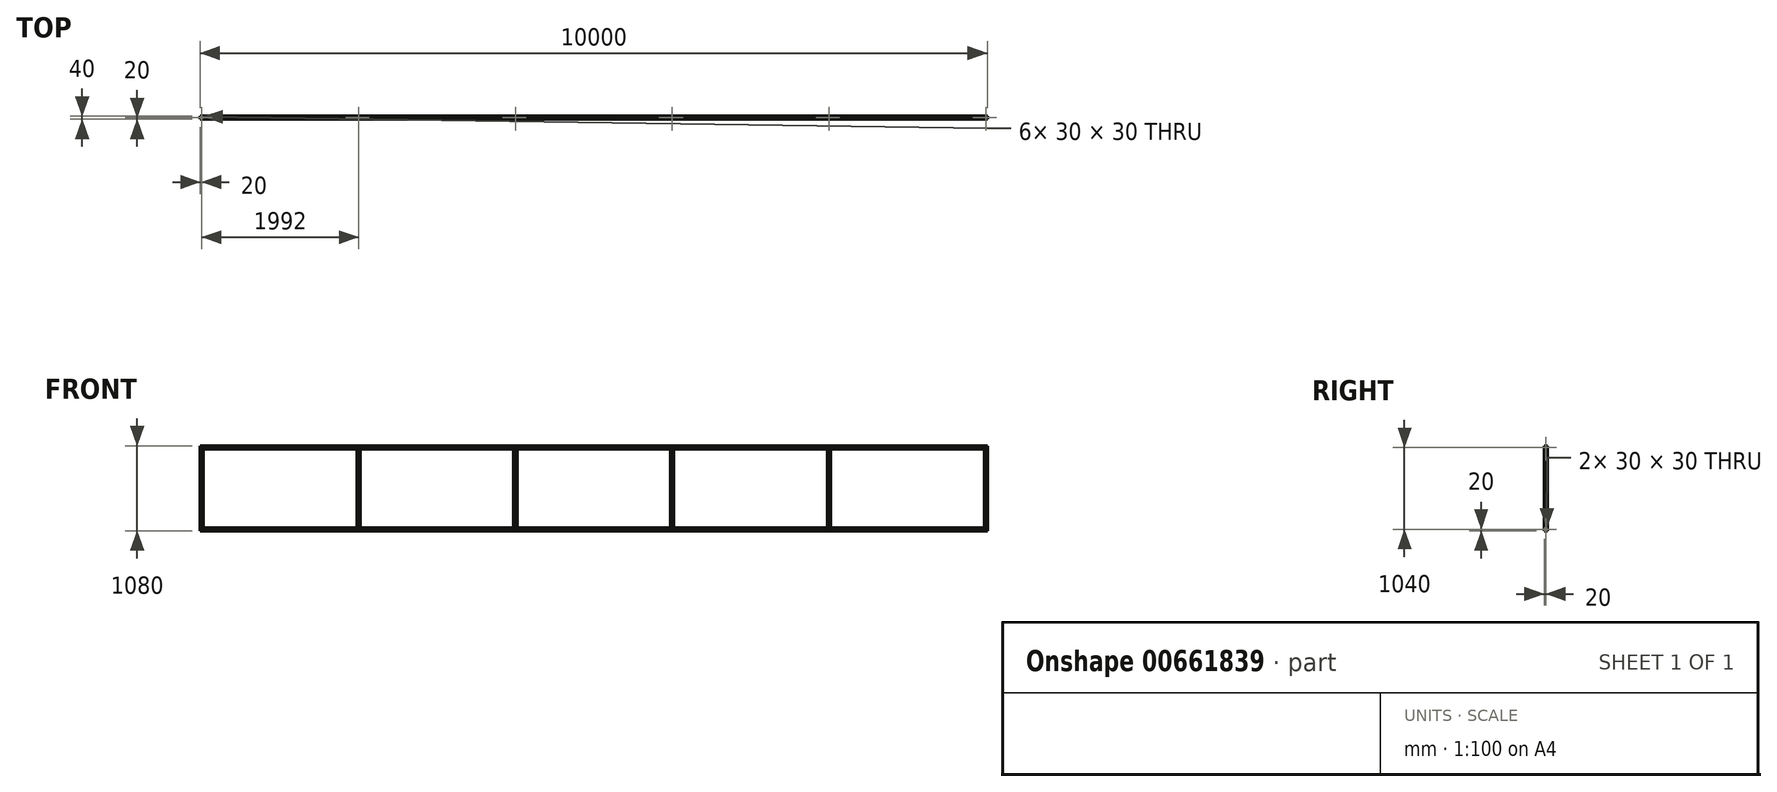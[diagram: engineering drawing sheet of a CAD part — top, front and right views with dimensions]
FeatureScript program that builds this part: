
annotation { "Feature Type Name" : "Feature", "Feature Type Description" : "" }
export const myFeature = defineFeature(function(context is Context, id is Id, definition is map)
    precondition{}
    {
        {
            var Q0;
            Q0=qCreatedBy(makeId("Top.planeOp"),FACE);
            var sketch = newSketch(context, id + "F0", { "sketchPlane" : qUnion([Q0])});
            skLineSegment(sketch, "E0", {"start": v(0, 0) * mm, "end": v(-5000, 0) * mm, "construction": true});
            skLineSegment(sketch, "E1", {"start": v(0, 0) * mm, "end": v(5000, 0) * mm, "construction": true});
            skLineSegment(sketch, "E2", {"start": v(-5000, 0) * mm, "end": v(-5000, 482.39) * mm, "construction": true});
            skLineSegment(sketch, "E3", {"start": v(5000, 0) * mm, "end": v(5000, 482.39) * mm, "construction": true});
            skLineSegment(sketch, "E4.bottom", {"start": v(-5000, 0) * mm, "end": v(-4960, 0) * mm});
            skLineSegment(sketch, "E4.top", {"start": v(-5000, -40) * mm, "end": v(-4960, -40) * mm});
            skLineSegment(sketch, "E4.left", {"start": v(-5000, 0) * mm, "end": v(-5000, -40) * mm});
            skLineSegment(sketch, "E4.right", {"start": v(-4960, 0) * mm, "end": v(-4960, -40) * mm});
            skLineSegment(sketch, "E5.0", {"start": v(-4995, -5) * mm, "end": v(-4965, -5) * mm});
            skLineSegment(sketch, "E5.1", {"start": v(-4995, -5) * mm, "end": v(-4995, -35) * mm});
            skLineSegment(sketch, "E5.2", {"start": v(-4995, -35) * mm, "end": v(-4965, -35) * mm});
            skLineSegment(sketch, "E5.3", {"start": v(-4965, -5) * mm, "end": v(-4965, -35) * mm});
            skLineSegment(sketch, "E6.1.0.0", {"start": v(-3008, -40) * mm, "end": v(-2968, -40) * mm});
            skLineSegment(sketch, "E6.1.0.1", {"start": v(-3008, 0) * mm, "end": v(-3008, -40) * mm});
            skLineSegment(sketch, "E6.1.0.2", {"start": v(-2968, 0) * mm, "end": v(-2968, -40) * mm});
            skLineSegment(sketch, "E6.1.0.3", {"start": v(-3008, 0) * mm, "end": v(-2968, 0) * mm});
            skLineSegment(sketch, "E6.1.0.4", {"start": v(-3003, -5) * mm, "end": v(-2973, -5) * mm});
            skLineSegment(sketch, "E6.1.0.5", {"start": v(-3003, -5) * mm, "end": v(-3003, -35) * mm});
            skLineSegment(sketch, "E6.1.0.6", {"start": v(-3003, -35) * mm, "end": v(-2973, -35) * mm});
            skLineSegment(sketch, "E6.1.0.7", {"start": v(-2973, -5) * mm, "end": v(-2973, -35) * mm});
            skLineSegment(sketch, "E6.2.0.0", {"start": v(-1016, -40) * mm, "end": v(-976, -40) * mm});
            skLineSegment(sketch, "E6.2.0.1", {"start": v(-1016, 0) * mm, "end": v(-1016, -40) * mm});
            skLineSegment(sketch, "E6.2.0.2", {"start": v(-976, 0) * mm, "end": v(-976, -40) * mm});
            skLineSegment(sketch, "E6.2.0.3", {"start": v(-1016, 0) * mm, "end": v(-976, 0) * mm});
            skLineSegment(sketch, "E6.2.0.4", {"start": v(-1011, -5) * mm, "end": v(-981, -5) * mm});
            skLineSegment(sketch, "E6.2.0.5", {"start": v(-1011, -5) * mm, "end": v(-1011, -35) * mm});
            skLineSegment(sketch, "E6.2.0.6", {"start": v(-1011, -35) * mm, "end": v(-981, -35) * mm});
            skLineSegment(sketch, "E6.2.0.7", {"start": v(-981, -5) * mm, "end": v(-981, -35) * mm});
            skLineSegment(sketch, "E6.direction1", {"start": v(-5000, -40) * mm, "end": v(-3008, -40) * mm, "construction": true});
            skLineSegment(sketch, "E7.0.3.0", {"start": v(976, -40) * mm, "end": v(1016, -40) * mm});
            skLineSegment(sketch, "E7.3.3.0", {"start": v(976, 0) * mm, "end": v(976, -40) * mm});
            skLineSegment(sketch, "E7.6.3.0", {"start": v(1016, 0) * mm, "end": v(1016, -40) * mm});
            skLineSegment(sketch, "E7.9.3.0", {"start": v(976, 0) * mm, "end": v(1016, 0) * mm});
            skLineSegment(sketch, "E7.12.3.0", {"start": v(981, -5) * mm, "end": v(1011, -5) * mm});
            skLineSegment(sketch, "E7.15.3.0", {"start": v(981, -5) * mm, "end": v(981, -35) * mm});
            skLineSegment(sketch, "E7.18.3.0", {"start": v(981, -35) * mm, "end": v(1011, -35) * mm});
            skLineSegment(sketch, "E7.21.3.0", {"start": v(1011, -5) * mm, "end": v(1011, -35) * mm});
            skLineSegment(sketch, "E7.0.4.0", {"start": v(2968, -40) * mm, "end": v(3008, -40) * mm});
            skLineSegment(sketch, "E7.3.4.0", {"start": v(2968, 0) * mm, "end": v(2968, -40) * mm});
            skLineSegment(sketch, "E7.6.4.0", {"start": v(3008, 0) * mm, "end": v(3008, -40) * mm});
            skLineSegment(sketch, "E7.9.4.0", {"start": v(2968, 0) * mm, "end": v(3008, 0) * mm});
            skLineSegment(sketch, "E7.12.4.0", {"start": v(2973, -5) * mm, "end": v(3003, -5) * mm});
            skLineSegment(sketch, "E7.15.4.0", {"start": v(2973, -5) * mm, "end": v(2973, -35) * mm});
            skLineSegment(sketch, "E7.18.4.0", {"start": v(2973, -35) * mm, "end": v(3003, -35) * mm});
            skLineSegment(sketch, "E7.21.4.0", {"start": v(3003, -5) * mm, "end": v(3003, -35) * mm});
            skLineSegment(sketch, "E7.0.5.0", {"start": v(4960, -40) * mm, "end": v(5000, -40) * mm});
            skLineSegment(sketch, "E7.3.5.0", {"start": v(4960, 0) * mm, "end": v(4960, -40) * mm});
            skLineSegment(sketch, "E7.6.5.0", {"start": v(5000, 0) * mm, "end": v(5000, -40) * mm});
            skLineSegment(sketch, "E7.9.5.0", {"start": v(4960, 0) * mm, "end": v(5000, 0) * mm});
            skLineSegment(sketch, "E7.12.5.0", {"start": v(4965, -5) * mm, "end": v(4995, -5) * mm});
            skLineSegment(sketch, "E7.15.5.0", {"start": v(4965, -5) * mm, "end": v(4965, -35) * mm});
            skLineSegment(sketch, "E7.18.5.0", {"start": v(4965, -35) * mm, "end": v(4995, -35) * mm});
            skLineSegment(sketch, "E7.21.5.0", {"start": v(4995, -5) * mm, "end": v(4995, -35) * mm});
            skSolve(sketch);
        }
        {
            var Q0;
            Q0 = qSketchRegion(id + "F0", true);
            extrude(context, id + "F1", {"entities" : qUnion([Q0]), "depth" : 1000 * mm, "offsetDistance" : 25 * mm});
        }
        {
            var Q0;
            Q0=makeQuery(id+"F1.opExtrude","SWEPT_FACE",FACE,{"disambiguationData":[OSD([sQuery(id+"F0.wireOp",EDGE,"E4.left")])]});
            var sketch = newSketch(context, id + "F2", { "sketchPlane" : qUnion([Q0])});
            skLineSegment(sketch, "E8.bottom", {"start": v(0, 1000) * mm, "end": v(40, 1000) * mm});
            skLineSegment(sketch, "E8.top", {"start": v(0, 1040) * mm, "end": v(40, 1040) * mm});
            skLineSegment(sketch, "E8.left", {"start": v(0, 1000) * mm, "end": v(0, 1040) * mm});
            skLineSegment(sketch, "E8.right", {"start": v(40, 1000) * mm, "end": v(40, 1040) * mm});
            skLineSegment(sketch, "E9.bottom", {"start": v(0, 0) * mm, "end": v(40, 0) * mm});
            skLineSegment(sketch, "E9.top", {"start": v(0, -40) * mm, "end": v(40, -40) * mm});
            skLineSegment(sketch, "E9.left", {"start": v(0, 0) * mm, "end": v(0, -40) * mm});
            skLineSegment(sketch, "E9.right", {"start": v(40, 0) * mm, "end": v(40, -40) * mm});
            skLineSegment(sketch, "E10.0", {"start": v(5, -35) * mm, "end": v(35, -35) * mm});
            skLineSegment(sketch, "E10.1", {"start": v(5, -5) * mm, "end": v(5, -35) * mm});
            skLineSegment(sketch, "E10.2", {"start": v(5, -5) * mm, "end": v(35, -5) * mm});
            skLineSegment(sketch, "E10.3", {"start": v(35, -5) * mm, "end": v(35, -35) * mm});
            skLineSegment(sketch, "E11.0", {"start": v(5, 1035) * mm, "end": v(35, 1035) * mm});
            skLineSegment(sketch, "E11.1", {"start": v(5, 1005) * mm, "end": v(5, 1035) * mm});
            skLineSegment(sketch, "E11.2", {"start": v(5, 1005) * mm, "end": v(35, 1005) * mm});
            skLineSegment(sketch, "E11.3", {"start": v(35, 1005) * mm, "end": v(35, 1035) * mm});
            skSolve(sketch);
        }
        {
            var Q0;
            Q0 = qSketchRegion(id + "F2", true);
            var Q1;
            Q1=makeQuery(id+"F1.opExtrude","SWEPT_FACE",FACE,{"disambiguationData":[OSD([sQuery(id+"F0.wireOp",EDGE,"E7.6.5.0")])]});
            extrude(context, id + "F3", {"entities" : qUnion([Q0]), "endBound" : BoundingType.UP_TO_SURFACE, "oppositeDirection" : true, "depth" : 25 * mm, "endBoundEntityFace" : qUnion([Q1]), "offsetDistance" : 25 * mm});
        }
    });
